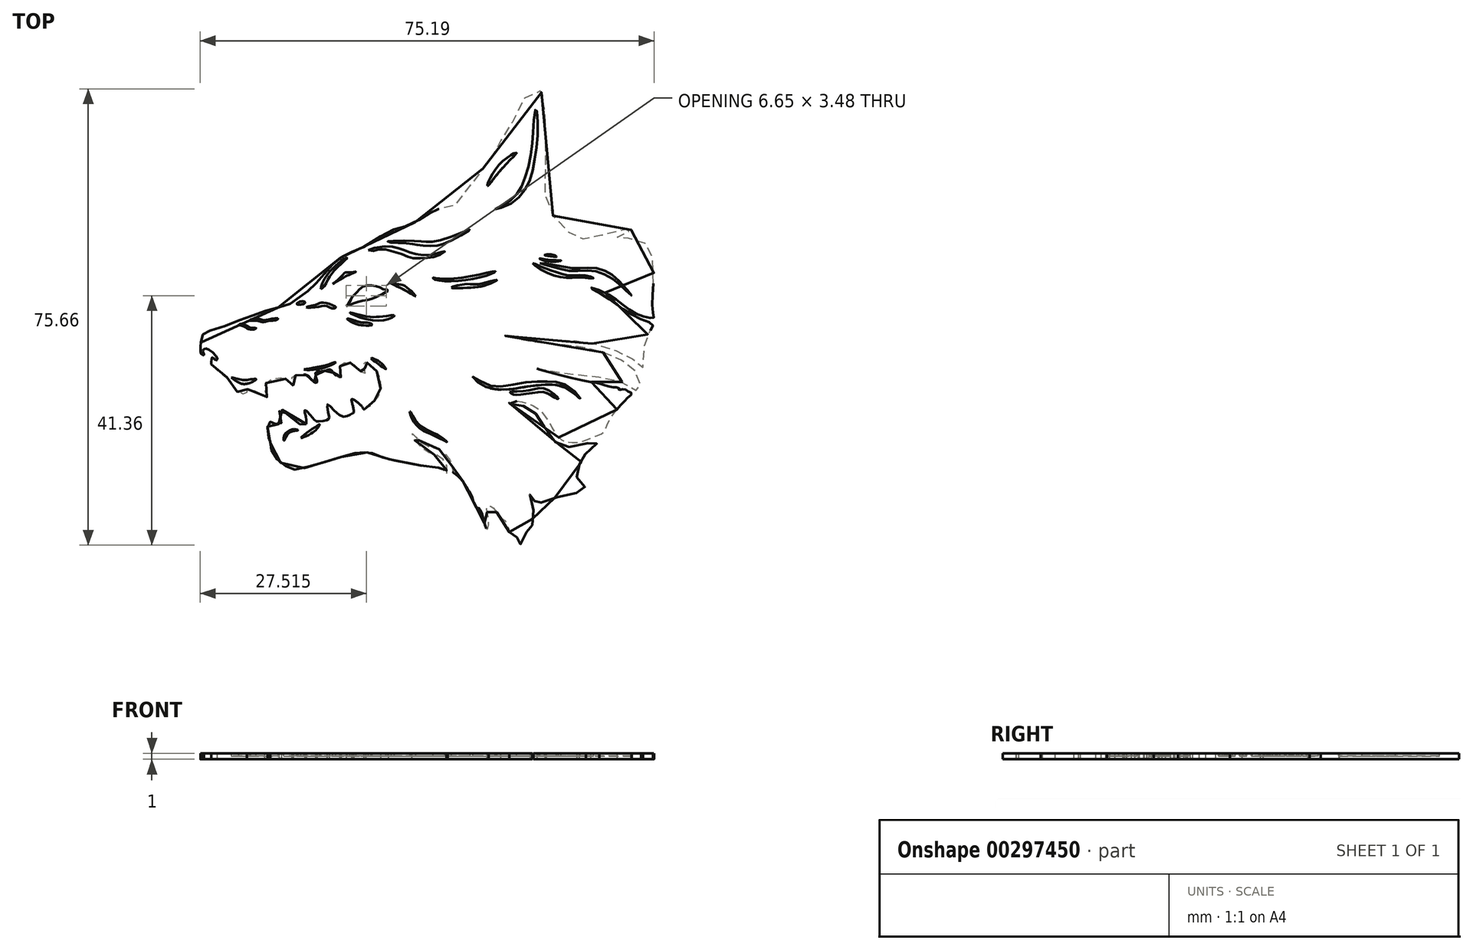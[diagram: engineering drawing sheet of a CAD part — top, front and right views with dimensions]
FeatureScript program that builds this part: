
annotation { "Feature Type Name" : "Feature", "Feature Type Description" : "" }
export const myFeature = defineFeature(function(context is Context, id is Id, definition is map)
    precondition{}
    {
        {
            var Q0;
            Q0=qCreatedBy(makeId("Top.planeOp"),FACE);
            var sketch = newSketch(context, id + "F0", { "sketchPlane" : qUnion([Q0])});
            skFitSpline(sketch, "E0", {"points": [v(1.7, 30.43) * mm, v(3.38, 28.83) * mm, v(5.2, 27.3) * mm, v(6.06, 25.78) * mm, v(7.8, 25.34) * mm, v(7.88, 25.85) * mm, v(8.31, 26.07) * mm, v(11.22, 24.76) * mm, v(11.07, 25.27) * mm, v(11, 27.01) * mm, v(13.61, 27.96) * mm, v(14.77, 27.3) * mm, v(15.35, 26.58) * mm, v(15.5, 26.58) * mm, v(15.35, 27.52) * mm, v(15.43, 28.18) * mm, v(16.37, 28.4) * mm, v(17, 28.43) * mm, v(17.55, 28.43) * mm, v(17.96, 28.27) * mm, v(18.59, 27.62) * mm, v(19.12, 27.13) * mm, v(19.44, 27.15) * mm, v(19.42, 27.68) * mm, v(19.24, 28.51) * mm, v(19.4, 28.9) * mm, v(20.48, 29.02) * mm, v(21.1, 29.22) * mm, v(21.7, 29.33) * mm, v(22.19, 28.8) * mm, v(22.7, 28.23) * mm, v(23.14, 27.94) * mm, v(23.4, 28.04) * mm, v(23.4, 28.65) * mm, v(23.25, 29.4) * mm, v(23.45, 30.14) * mm, v(24.26, 30.44) * mm, v(25.06, 30.42) * mm, v(26, 29.77) * mm, v(26.7, 29.04) * mm, v(27.2, 28.72) * mm, v(27.52, 28.72) * mm, v(27.39, 29.25) * mm, v(27.22, 30.2) * mm, v(27.4, 30.5) * mm, v(27.74, 30.5) * mm, v(28.42, 29.93) * mm, v(29.03, 29.46) * mm, v(29.87, 27.94) * mm, v(30.01, 26.04) * mm, v(29.78, 25) * mm, v(28.96, 24.06) * mm, v(28.41, 23.41) * mm, v(27.3, 22.69) * mm, v(26.95, 23.14) * mm, v(25.28, 24.38) * mm, v(25.2, 24.13) * mm, v(25.55, 22.14) * mm, v(25.18, 22.02) * mm], "startDerivative": vector(55.33, -59.39) * mm, "endDerivative": vector(-41.24, 3.28) * mm});
            skFitSpline(sketch, "E1", {"points": [v(25.34, 22) * mm, v(24.77, 21.7) * mm, v(23.5, 21.58) * mm, v(21.4, 23.42) * mm, v(21.16, 23.42) * mm, v(21.5, 21.3) * mm, v(21.36, 21.04) * mm, v(20.77, 20.78) * mm, v(19.52, 20.67) * mm, v(19.24, 20.76) * mm, v(17.57, 22.55) * mm, v(17.42, 22.5) * mm, v(17.6, 21.54) * mm, v(17.68, 20.28) * mm], "startDerivative": vector(-8.04, -4.42) * mm, "endDerivative": vector(-0.22, -13.93) * mm});
            skLineSegment(sketch, "E2", {"start": v(25.34, 22) * mm, "end": v(25.34, 22.01) * mm});
            skFitSpline(sketch, "E3", {"points": [v(27.3, 22.69) * mm, v(27.06, 22.75) * mm, v(25.28, 24.38) * mm, v(25.06, 24.13) * mm], "startDerivative": vector(-0.91, -0.23) * mm, "endDerivative": vector(-0.56, -1.9) * mm});
            skFitSpline(sketch, "E4", {"points": [v(17.68, 20.28) * mm, v(17.25, 20.09) * mm, v(16.58, 20.28) * mm, v(13.38, 22.77) * mm, v(13.2, 22.67) * mm, v(13.58, 20.69) * mm, v(13.43, 20.28) * mm, v(12.9, 20.28) * mm, v(12.33, 20.28) * mm, v(11.93, 20.59) * mm, v(11.4, 20.49) * mm, v(11.28, 19.71) * mm, v(11.43, 18.16) * mm, v(11.58, 17.84) * mm, v(11.73, 17.84) * mm, v(11.75, 17.36) * mm, v(11.78, 16.46) * mm, v(12.35, 15.14) * mm, v(13.43, 13.91) * mm, v(14.75, 12.99) * mm, v(15.85, 12.71) * mm, v(18.9, 13.41) * mm, v(22.66, 14.51) * mm, v(25.58, 15.39) * mm, v(27.16, 15.54) * mm, v(27.9, 15.54) * mm, v(28.7, 15.39) * mm, v(30.18, 14.76) * mm, v(32.2, 14.28) * mm, v(34.86, 13.7) * mm, v(37.27, 13.3) * mm, v(38.25, 13.16) * mm, v(38.84, 12.98) * mm, v(39.46, 13.03) * mm, v(40, 12.83) * mm, v(40.5, 12.57) * mm, v(41.02, 11.95) * mm, v(41.15, 11.95) * mm, v(40.94, 12.75) * mm, v(41.02, 13.4) * mm, v(40, 14.72) * mm, v(38.64, 15.29) * mm, v(37.14, 16.09) * mm, v(35.97, 17.28) * mm, v(35.5, 17.77) * mm, v(35.2, 18.55) * mm, v(35.35, 18.7) * mm, v(35.84, 18.08) * mm, v(37.06, 17) * mm, v(38.71, 16.3) * mm, v(39.52, 16.2) * mm, v(40.21, 15.7) * mm, v(41.07, 14.92) * mm, v(41.74, 13.78) * mm, v(41.92, 12.8) * mm, v(42, 12.3) * mm, v(42.85, 11.59) * mm, v(43.79, 10.58) * mm, v(44.33, 9.6) * mm, v(45, 8.6) * mm, v(45.85, 6.45) * mm, v(46.23, 6.34) * mm, v(46.85, 5.3) * mm, v(47.6, 2.81) * mm, v(47.74, 2.81) * mm, v(47.87, 4.86) * mm, v(47.6, 6.04) * mm, v(47.72, 6.58) * mm, v(48.1, 6.7) * mm, v(48.95, 6.04) * mm, v(50.1, 4.63) * mm, v(50.74, 4.07) * mm, v(51.38, 2.33) * mm], "startDerivative": vector(-47.47, -25.3) * mm, "endDerivative": vector(30.8, -113.8) * mm});
            skPoint(sketch, "E5.118.internal.snap0", {"position": v(76.24, 37.9) * mm});
            skPoint(sketch, "E5.119.internal.snap0", {"position": v(76.24, 37.9) * mm});
            skPoint(sketch, "E5.153.internal.snap0", {"position": v(38.12, 0) * mm});
            skPoint(sketch, "E5.171.internal.snap0", {"position": v(0, 37.9) * mm});
            skFitSpline(sketch, "E5", {"points": [v(51.38, 2.33) * mm, v(52.06, 2.33) * mm, v(52.36, 1.9) * mm, v(52.6, 1.43) * mm, v(52.8, 1.1) * mm, v(52.92, 0.25) * mm, v(53.12, 0.21) * mm, v(53.66, 1.5) * mm, v(54.07, 1.98) * mm, v(54.26, 2.58) * mm, v(54.75, 3.18) * mm, v(55.17, 3.35) * mm, v(55.18, 3.53) * mm, v(55.15, 4.7) * mm, v(55.38, 6.02) * mm, v(55.2, 6.95) * mm, v(54.78, 8.57) * mm, v(55.02, 8.81) * mm, v(55.33, 8.33) * mm, v(55.6, 7.3) * mm, v(55.76, 6.45) * mm, v(56.55, 7.16) * mm, v(58.12, 7.8) * mm, v(59.55, 8.21) * mm, v(61.96, 8.76) * mm, v(62.99, 9) * mm, v(64.02, 9.53) * mm, v(64, 9.7) * mm, v(63.32, 10.2) * mm, v(62.75, 10.43) * mm, v(62.63, 12.25) * mm, v(62.92, 12.68) * mm, v(62.97, 13.63) * mm, v(63.35, 14.04) * mm, v(63.6, 14.85) * mm, v(64.16, 15.5) * mm, v(64.65, 16.09) * mm, v(66.22, 17.33) * mm, v(66.22, 17.46) * mm, v(64.62, 17.15) * mm, v(62.85, 16.54) * mm, v(60.72, 16.52) * mm, v(59.68, 16.82) * mm, v(58.72, 17.5) * mm, v(57.5, 19.13) * mm, v(56.62, 20.79) * mm, v(55.91, 21.75) * mm, v(55.2, 22.49) * mm, v(54.24, 23.03) * mm, v(52.9, 23.5) * mm, v(51.74, 23.62) * mm, v(51.38, 23.67) * mm, v(51.38, 24.04) * mm, v(51.57, 24.02) * mm, v(52.59, 24.07) * mm, v(53.84, 23.86) * mm, v(55.35, 23.26) * mm, v(56.46, 22.53) * mm, v(57.38, 21.45) * mm, v(58.32, 19.91) * mm, v(58.98, 18.7) * mm, v(59.76, 17.81) * mm, v(60.85, 17.3) * mm, v(62.43, 17.2) * mm, v(63.94, 17.55) * mm, v(65.88, 18.33) * mm, v(67, 18.9) * mm, v(67.6, 20.17) * mm, v(68.26, 21.44) * mm, v(69.56, 23.1) * mm, v(71.1, 24.72) * mm, v(71.63, 25.37) * mm, v(70.94, 25.74) * mm, v(70.42, 26.04) * mm, v(69.6, 25.92) * mm, v(69.45, 26.25) * mm, v(68.92, 26.37) * mm, v(67.87, 26.46) * mm, v(66.33, 26.96) * mm, v(62.84, 27.6) * mm, v(55.94, 29.49) * mm, v(63, 28.3) * mm, v(67.4, 27.94) * mm, v(70.32, 27.1) * mm, v(72.16, 26.04) * mm, v(73.12, 25.23) * mm, v(72.97, 27.52) * mm, v(72.46, 28.68) * mm, v(71.48, 29.8) * mm, v(69.62, 31) * mm, v(67.3, 32) * mm, v(63.91, 32.9) * mm, v(60.82, 33.31) * mm, v(57.23, 33.66) * mm, v(54.97, 33.91) * mm, v(52.7, 34.32) * mm, v(51.38, 34.58) * mm, v(49.9, 35.43) * mm, v(52.1, 34.8) * mm, v(55.2, 34.36) * mm, v(58.96, 34.17) * mm, v(61.68, 34.1) * mm, v(64.09, 33.77) * mm, v(66.62, 33.26) * mm, v(69.45, 32.3) * mm, v(71.5, 31.35) * mm, v(73.33, 29.2) * mm, v(73.51, 31.1) * mm, v(73.96, 34.03) * mm, v(74.45, 35.4) * mm, v(75.14, 36.65) * mm, v(73.37, 37.6) * mm, v(69.77, 39.62) * mm, v(67.1, 41.51) * mm, v(64.83, 42.87) * mm, v(67.13, 42.07) * mm, v(70.06, 40.13) * mm, v(72.28, 38.62) * mm, v(74.52, 37.9) * mm, v(75.3, 37.9) * mm, v(75.1, 38.84) * mm, v(75.2, 42.72) * mm, v(75.13, 47.74) * mm, v(74.42, 49.57) * mm, v(73.55, 50.44) * mm, v(71.42, 51.03) * mm, v(69.94, 50.99) * mm, v(69.2, 51.12) * mm, v(70.02, 51.58) * mm, v(70.81, 52) * mm, v(71.7, 52.65) * mm, v(71.7, 52.88) * mm, v(69.55, 52.1) * mm, v(65.64, 51.41) * mm, v(63.64, 50.97) * mm, v(62.22, 50.87) * mm, v(60.24, 53.45) * mm, v(58.2, 55.28) * mm, v(57.23, 59.62) * mm, v(57.45, 64.42) * mm, v(57.28, 70.15) * mm, v(57.19, 73.48) * mm, v(56.14, 75.78) * mm, v(53.97, 74.4) * mm, v(51.79, 70.21) * mm, v(50.22, 67.75) * mm, v(48.96, 65.22) * mm, v(47.95, 64) * mm, v(45.85, 61.03) * mm, v(44.25, 59.06) * mm, v(42.77, 56.97) * mm, v(41.16, 55.92) * mm, v(39.46, 55.92) * mm, v(38.12, 55.2) * mm, v(36.36, 54.07) * mm, v(33.69, 52.9) * mm, v(31.9, 52.39) * mm, v(29.46, 51.03) * mm, v(28.44, 50.39) * mm, v(27.52, 49.75) * mm, v(25.48, 48.9) * mm, v(24.2, 48.35) * mm, v(22.65, 47.27) * mm, v(21.23, 45.8) * mm, v(19.86, 44.25) * mm, v(18.56, 42.79) * mm, v(17.36, 41.86) * mm, v(16.32, 41.1) * mm, v(14.69, 40.01) * mm, v(12.9, 39.55) * mm, v(10.55, 38.86) * mm, v(7.88, 37.9) * mm, v(5.5, 37.03) * mm, v(2.22, 35.83) * mm, v(0.84, 35.53) * mm, v(0.46, 34.75) * mm, v(0.27, 33.87) * mm, v(0, 32.43) * mm], "startDerivative": vector(214.49, 36.32) * mm, "endDerivative": vector(-54.5, -292.94) * mm});
            skFitSpline(sketch, "E6", {"points": [v(1.97, 30.14) * mm, v(2.02, 31.1) * mm, v(2.14, 31.3) * mm, v(2.7, 30.84) * mm, v(3, 31.03) * mm, v(1.38, 32.7) * mm, v(0.75, 32.7) * mm, v(0.58, 32.5) * mm, v(0.58, 32.2) * mm, v(0.73, 31.94) * mm, v(0.7, 31.69) * mm, v(0.5, 31.75) * mm, v(0.2, 32.2) * mm, v(0.25, 33.76) * mm], "startDerivative": vector(-0.09, 10.6) * mm, "endDerivative": vector(1.95, 14.03) * mm});
            skFitSpline(sketch, "E7", {"points": [v(5.25, 27.96) * mm, v(6.64, 27.07) * mm, v(7.44, 26.88) * mm, v(8.42, 27.07) * mm], "startDerivative": vector(3.66, -2.61) * mm, "endDerivative": vector(3.26, 0.84) * mm});
            skFitSpline(sketch, "E8", {"points": [v(8.42, 27.07) * mm, v(9.07, 27.42) * mm, v(9.4, 27.7) * mm, v(8.25, 27.63) * mm, v(7.2, 27.56) * mm, v(5.84, 27.87) * mm, v(5.25, 27.96) * mm], "startDerivative": vector(4.1, 2.1) * mm, "endDerivative": vector(-3.68, 0.4) * mm});
            skFitSpline(sketch, "E9", {"points": [v(6.54, 36.72) * mm, v(7.23, 36.5) * mm, v(8.01, 36.05) * mm, v(9.1, 35.95) * mm, v(9.4, 36.13) * mm, v(8.55, 36.2) * mm, v(8, 36.5) * mm, v(7.37, 36.76) * mm, v(7.06, 36.88) * mm, v(6.54, 36.72) * mm]});
            skFitSpline(sketch, "E10", {"points": [v(8.31, 37.42) * mm, v(9.56, 37.4) * mm, v(10.55, 37.12) * mm, v(11.41, 37.34) * mm, v(12.34, 37.42) * mm, v(13.04, 37.72) * mm, v(12.01, 37.74) * mm, v(10.79, 37.48) * mm, v(9.88, 37.68) * mm, v(8.88, 37.7) * mm, v(8.31, 37.42) * mm]});
            skFitSpline(sketch, "E11", {"points": [v(16.13, 40.18) * mm, v(17.12, 40.14) * mm, v(17.5, 40.4) * mm, v(17.03, 40.61) * mm, v(16.13, 40.18) * mm]});
            skFitSpline(sketch, "E12", {"points": [v(17.72, 39.62) * mm, v(19.31, 39.62) * mm, v(20.95, 39.88) * mm, v(22.16, 39.4) * mm, v(22.59, 39.62) * mm, v(21.2, 40.27) * mm, v(20.09, 40.4) * mm, v(19.44, 40.1) * mm, v(17.72, 39.62) * mm]});
            skFitSpline(sketch, "E13", {"points": [v(24.48, 37.68) * mm, v(25.99, 36.82) * mm, v(27.37, 36.6) * mm, v(28.61, 36.7) * mm, v(28.06, 37.04) * mm, v(26.94, 37.08) * mm, v(25.26, 37.56) * mm, v(24.48, 37.68) * mm]});
            skFitSpline(sketch, "E14", {"points": [v(20.14, 42.7) * mm, v(20.78, 44.41) * mm, v(22.43, 46.42) * mm, v(23.8, 47.5) * mm, v(24.5, 47.82) * mm, v(22.9, 46.28) * mm, v(21.46, 44.52) * mm, v(20.57, 42.98) * mm, v(20.14, 42.7) * mm]});
            skFitSpline(sketch, "E15", {"points": [v(24.33, 39.8) * mm, v(25.08, 40.11) * mm, v(26.44, 40.54) * mm, v(28.05, 40.9) * mm, v(29.34, 41.37) * mm, v(31.31, 42.48) * mm, v(30.67, 42.55) * mm, v(29.77, 42.94) * mm, v(28.73, 43.23) * mm, v(27.34, 43.16) * mm, v(26.37, 42.48) * mm, v(25.69, 41.69) * mm, v(25.22, 41.26) * mm, v(24.97, 40.54) * mm, v(24.33, 39.8) * mm]});
            skFitSpline(sketch, "E16", {"points": [v(22.07, 43.48) * mm, v(23.5, 44.7) * mm, v(24.15, 45.38) * mm, v(24.8, 45.38) * mm, v(25.94, 45.52) * mm, v(24.86, 45.02) * mm, v(24.08, 44.66) * mm, v(22.07, 43.48) * mm]});
            skFitSpline(sketch, "E17", {"points": [v(24.97, 38.72) * mm, v(27.3, 38.18) * mm, v(29.16, 38) * mm, v(30.7, 38.14) * mm, v(32.32, 38.25) * mm, v(31.57, 37.71) * mm, v(27.3, 37.75) * mm, v(24.97, 38.72) * mm]});
            skFitSpline(sketch, "E18", {"points": [v(35.86, 41.44) * mm, v(34.4, 42.9) * mm, v(33.07, 43.45) * mm, v(31.78, 43.59) * mm, v(34.04, 42.48) * mm, v(35.86, 41.44) * mm]});
            skFitSpline(sketch, "E19", {"points": [v(28.01, 49.07) * mm, v(28.88, 48.99) * mm, v(29.96, 49.23) * mm, v(32.1, 48.88) * mm, v(34.24, 48.15) * mm, v(35.22, 47.8) * mm, v(36.99, 47.75) * mm, v(38.53, 47.88) * mm, v(40.09, 48.45) * mm, v(40.69, 48.95) * mm, v(38.8, 48.37) * mm, v(36.3, 48.37) * mm, v(34.98, 48.66) * mm, v(33.68, 49.2) * mm, v(32.35, 49.56) * mm, v(30.4, 49.69) * mm, v(28.01, 49.07) * mm]});
            skFitSpline(sketch, "E20", {"points": [v(31.23, 50.53) * mm, v(35.48, 50.64) * mm, v(37.47, 50.47) * mm, v(40.51, 50.9) * mm, v(44.9, 52.52) * mm, v(41.32, 50.53) * mm, v(38.93, 49.83) * mm, v(36.29, 49.94) * mm, v(35.08, 50.15) * mm, v(31.95, 50.34) * mm, v(31.23, 50.53) * mm]});
            skFitSpline(sketch, "E21", {"points": [v(47.75, 59.77) * mm, v(49.5, 63.08) * mm, v(52.56, 65.23) * mm, v(50.04, 62.5) * mm, v(47.75, 59.77) * mm]});
            skFitSpline(sketch, "E22", {"points": [v(49, 55.89) * mm, v(50.87, 56.45) * mm, v(53.33, 58.26) * mm, v(54.88, 61.07) * mm, v(55.7, 65.04) * mm, v(56.1, 70) * mm, v(55.75, 72.56) * mm, v(55.4, 70) * mm, v(55.06, 65.78) * mm, v(54.1, 61.54) * mm, v(52.94, 58.87) * mm, v(51.17, 57.1) * mm, v(49, 55.89) * mm]});
            skFitSpline(sketch, "E23", {"points": [v(39.04, 44.23) * mm, v(43.18, 44.03) * mm, v(48.28, 45.11) * mm, v(49.04, 45.57) * mm, v(44.14, 44.62) * mm, v(39.18, 44.42) * mm, v(38.69, 44.5) * mm, v(39.04, 44.23) * mm]});
            skFitSpline(sketch, "E24", {"points": [v(41.8, 42.87) * mm, v(44.65, 42.85) * mm, v(47.65, 43.34) * mm, v(49.3, 44.15) * mm, v(46.19, 43.46) * mm, v(44.14, 43.46) * mm, v(41.8, 42.87) * mm]});
            skFitSpline(sketch, "E25", {"points": [v(57.21, 48.28) * mm, v(58.28, 48.38) * mm, v(59.18, 48.01) * mm, v(58.11, 48.11) * mm, v(57.21, 48.28) * mm]});
            skFitSpline(sketch, "E26", {"points": [v(56.34, 47.68) * mm, v(57.98, 47.2) * mm, v(59.95, 47.34) * mm, v(57.95, 47.48) * mm, v(56.34, 47.68) * mm]});
            skFitSpline(sketch, "E27", {"points": [v(56.44, 46.94) * mm, v(59.58, 46.04) * mm, v(61.81, 45.64) * mm, v(64.38, 45.7) * mm, v(66.42, 45.38) * mm, v(68.72, 44.17) * mm, v(70.18, 42.84) * mm, v(71.62, 41.57) * mm, v(69.82, 43.7) * mm, v(67.95, 45.28) * mm, v(65.95, 46.04) * mm, v(63.82, 46.18) * mm, v(62.11, 46.1) * mm, v(59.85, 46.4) * mm, v(57.85, 46.8) * mm, v(56.44, 46.94) * mm]});
            skFitSpline(sketch, "E28", {"points": [v(55.24, 46.9) * mm, v(57.21, 45.54) * mm, v(60.55, 44.54) * mm, v(63.48, 44.54) * mm, v(65.32, 44.4) * mm, v(63.98, 44.9) * mm, v(61.45, 44.88) * mm, v(58.75, 45.58) * mm, v(56.58, 46.38) * mm, v(55.24, 46.9) * mm]});
            skFitSpline(sketch, "E29", {"points": [v(45.34, 28.08) * mm, v(47.3, 26.97) * mm, v(50.14, 26.53) * mm, v(54.2, 27.18) * mm, v(57.24, 27.27) * mm, v(59.24, 27.21) * mm, v(61.8, 26.05) * mm, v(63.12, 24.5) * mm, v(61.27, 25.93) * mm, v(59.12, 26.73) * mm, v(56.35, 26.7) * mm, v(53.27, 26.29) * mm, v(50.4, 25.96) * mm, v(48.17, 26.2) * mm, v(46.47, 26.91) * mm, v(45.34, 28.08) * mm]});
            skFitSpline(sketch, "E30", {"points": [v(51.4, 25.6) * mm, v(52.77, 25.63) * mm, v(55.72, 26.1) * mm, v(57.78, 25.93) * mm, v(59.48, 24.44) * mm, v(58.32, 24.97) * mm, v(57.12, 25.54) * mm, v(54.53, 25.33) * mm, v(52.35, 25.1) * mm, v(51.84, 25.21) * mm, v(51.4, 25.6) * mm]});
            skFitSpline(sketch, "E31", {"points": [v(34.95, 22.31) * mm, v(36.15, 20.45) * mm, v(37.73, 19.25) * mm, v(39.62, 18.37) * mm, v(41.07, 17.28) * mm, v(39.6, 17.98) * mm, v(37.83, 18.8) * mm, v(36.49, 19.55) * mm, v(35.29, 21) * mm, v(34.85, 22.38) * mm], "startDerivative": vector(8.84, -16.2) * mm, "endDerivative": vector(-2.93, 13.91) * mm});
            skLineSegment(sketch, "E32", {"start": v(34.95, 22.31) * mm, "end": v(34.85, 22.38) * mm});
            skFitSpline(sketch, "E33", {"points": [v(28.44, 31.15) * mm, v(29.72, 30.68) * mm, v(30.89, 29.35) * mm, v(29.6, 30.25) * mm, v(28.44, 31.15) * mm]});
            skFitSpline(sketch, "E34", {"points": [v(16.83, 17.97) * mm, v(18.45, 18.63) * mm, v(19.54, 19.57) * mm, v(19.92, 20.19) * mm, v(18.24, 19.1) * mm, v(16.83, 17.97) * mm]});
            skFitSpline(sketch, "E35", {"points": [v(13.94, 17.7) * mm, v(14.08, 18.48) * mm, v(14.8, 19.08) * mm, v(15.7, 19.43) * mm, v(16.34, 19.23) * mm, v(15.42, 19.02) * mm, v(14.41, 18.3) * mm, v(14.01, 17.52) * mm, v(13.94, 17.7) * mm]});
            skFitSpline(sketch, "E36", {"points": [v(17.35, 29.31) * mm, v(20.15, 29.82) * mm, v(22.58, 30.49) * mm, v(20.1, 29.45) * mm, v(17.35, 29.31) * mm]});
            skSolve(sketch);
        }
        {
            var Q0;
            Q0 = qSketchRegion(id + "F0", true);
            extrude(context, id + "F1", {"entities" : qUnion([Q0]), "depth" : 1 * mm});
        }
        {
            var Q0;
            Q0=makeQuery(id+"F0.imprint","IMPRINT",FACE,{"disambiguationData":[TD([[makeQuery(id+"F0.imprint","IMPRINT",EDGE,{"derivedFrom":sQuery(id+"F0.wireOp",EDGE,"E16")}),-1.0]])]});
            var Q1;
            Q1=makeQuery(id+"F0.imprint","IMPRINT",FACE,{"disambiguationData":[TD([[makeQuery(id+"F0.imprint","IMPRINT",EDGE,{"derivedFrom":sQuery(id+"F0.wireOp",EDGE,"E14")}),-1.0]])]});
            var Q2;
            Q2=makeQuery(id+"F0.imprint","IMPRINT",FACE,{"disambiguationData":[TD([[makeQuery(id+"F0.imprint","IMPRINT",EDGE,{"derivedFrom":sQuery(id+"F0.wireOp",EDGE,"E18")}),1.0]])]});
            var Q3;
            Q3=makeQuery(id+"F0.imprint","IMPRINT",FACE,{"disambiguationData":[TD([[makeQuery(id+"F0.imprint","IMPRINT",EDGE,{"derivedFrom":sQuery(id+"F0.wireOp",EDGE,"E19")}),1.0]])]});
            var Q4;
            Q4=makeQuery(id+"F0.imprint","IMPRINT",FACE,{"disambiguationData":[TD([[makeQuery(id+"F0.imprint","IMPRINT",EDGE,{"derivedFrom":sQuery(id+"F0.wireOp",EDGE,"E20")}),-1.0]])]});
            var Q5;
            Q5=makeQuery(id+"F0.imprint","IMPRINT",FACE,{"disambiguationData":[TD([[makeQuery(id+"F0.imprint","IMPRINT",EDGE,{"derivedFrom":sQuery(id+"F0.wireOp",EDGE,"E23")}),1.0]])]});
            var Q6;
            Q6=makeQuery(id+"F0.imprint","IMPRINT",FACE,{"disambiguationData":[TD([[makeQuery(id+"F0.imprint","IMPRINT",EDGE,{"derivedFrom":sQuery(id+"F0.wireOp",EDGE,"E24")}),1.0]])]});
            var Q7;
            Q7=makeQuery(id+"F0.imprint","IMPRINT",FACE,{"disambiguationData":[TD([[makeQuery(id+"F0.imprint","IMPRINT",EDGE,{"derivedFrom":sQuery(id+"F0.wireOp",EDGE,"E17")}),-1.0]])]});
            var Q8;
            Q8=makeQuery(id+"F0.imprint","IMPRINT",FACE,{"disambiguationData":[TD([[makeQuery(id+"F0.imprint","IMPRINT",EDGE,{"derivedFrom":sQuery(id+"F0.wireOp",EDGE,"E13")}),1.0]])]});
            var Q9;
            Q9=makeQuery(id+"F0.imprint","IMPRINT",FACE,{"disambiguationData":[TD([[makeQuery(id+"F0.imprint","IMPRINT",EDGE,{"derivedFrom":sQuery(id+"F0.wireOp",EDGE,"E12")}),1.0]])]});
            var Q10;
            Q10=makeQuery(id+"F0.imprint","IMPRINT",FACE,{"disambiguationData":[TD([[makeQuery(id+"F0.imprint","IMPRINT",EDGE,{"derivedFrom":sQuery(id+"F0.wireOp",EDGE,"E10")}),1.0]])]});
            var Q11;
            Q11=makeQuery(id+"F0.imprint","IMPRINT",FACE,{"disambiguationData":[TD([[makeQuery(id+"F0.imprint","IMPRINT",EDGE,{"derivedFrom":sQuery(id+"F0.wireOp",EDGE,"E9")}),1.0]])]});
            var Q12;
            Q12=makeQuery(id+"F0.imprint","IMPRINT",FACE,{"disambiguationData":[TD([[makeQuery(id+"F0.imprint","IMPRINT",EDGE,{"derivedFrom":sQuery(id+"F0.wireOp",EDGE,"E7")}),1.0]])]});
            var Q13;
            Q13=makeQuery(id+"F0.imprint","IMPRINT",FACE,{"disambiguationData":[TD([[makeQuery(id+"F0.imprint","IMPRINT",EDGE,{"derivedFrom":sQuery(id+"F0.wireOp",EDGE,"E36")}),-1.0]])]});
            var Q14;
            Q14=makeQuery(id+"F0.imprint","IMPRINT",FACE,{"disambiguationData":[TD([[makeQuery(id+"F0.imprint","IMPRINT",EDGE,{"derivedFrom":sQuery(id+"F0.wireOp",EDGE,"E33")}),-1.0]])]});
            var Q15;
            Q15=makeQuery(id+"F0.imprint","IMPRINT",FACE,{"disambiguationData":[TD([[makeQuery(id+"F0.imprint","IMPRINT",EDGE,{"derivedFrom":sQuery(id+"F0.wireOp",EDGE,"E34")}),1.0]])]});
            var Q16;
            Q16=makeQuery(id+"F0.imprint","IMPRINT",FACE,{"disambiguationData":[TD([[makeQuery(id+"F0.imprint","IMPRINT",EDGE,{"derivedFrom":sQuery(id+"F0.wireOp",EDGE,"E35")}),-1.0]])]});
            var Q17;
            Q17=makeQuery(id+"F0.imprint","IMPRINT",FACE,{"disambiguationData":[TD([[makeQuery(id+"F0.imprint","IMPRINT",EDGE,{"derivedFrom":sQuery(id+"F0.wireOp",EDGE,"E31")}),-1.0]])]});
            var Q18;
            Q18=makeQuery(id+"F0.imprint","IMPRINT",FACE,{"disambiguationData":[TD([[makeQuery(id+"F0.imprint","IMPRINT",EDGE,{"derivedFrom":sQuery(id+"F0.wireOp",EDGE,"E29")}),-1.0]])]});
            var Q19;
            Q19=makeQuery(id+"F0.imprint","IMPRINT",FACE,{"disambiguationData":[TD([[makeQuery(id+"F0.imprint","IMPRINT",EDGE,{"derivedFrom":sQuery(id+"F0.wireOp",EDGE,"E30")}),-1.0]])]});
            var Q20;
            Q20=makeQuery(id+"F0.imprint","IMPRINT",FACE,{"disambiguationData":[TD([[makeQuery(id+"F0.imprint","IMPRINT",EDGE,{"derivedFrom":sQuery(id+"F0.wireOp",EDGE,"E28")}),1.0]])]});
            var Q21;
            Q21=makeQuery(id+"F0.imprint","IMPRINT",FACE,{"disambiguationData":[TD([[makeQuery(id+"F0.imprint","IMPRINT",EDGE,{"derivedFrom":sQuery(id+"F0.wireOp",EDGE,"E27")}),1.0]])]});
            var Q22;
            Q22=makeQuery(id+"F0.imprint","IMPRINT",FACE,{"disambiguationData":[TD([[makeQuery(id+"F0.imprint","IMPRINT",EDGE,{"derivedFrom":sQuery(id+"F0.wireOp",EDGE,"E26")}),1.0]])]});
            var Q23;
            Q23=makeQuery(id+"F0.imprint","IMPRINT",FACE,{"disambiguationData":[TD([[makeQuery(id+"F0.imprint","IMPRINT",EDGE,{"derivedFrom":sQuery(id+"F0.wireOp",EDGE,"E21")}),-1.0]])]});
            var Q24;
            Q24=makeQuery(id+"F0.imprint","IMPRINT",FACE,{"disambiguationData":[TD([[makeQuery(id+"F0.imprint","IMPRINT",EDGE,{"derivedFrom":sQuery(id+"F0.wireOp",EDGE,"E22")}),1.0]])]});
            var Q25;
            Q25=makeQuery(id+"F0.imprint","IMPRINT",FACE,{"disambiguationData":[TD([[makeQuery(id+"F0.imprint","IMPRINT",EDGE,{"derivedFrom":sQuery(id+"F0.wireOp",EDGE,"E25")}),-1.0]])]});
            var Q26;
            Q26=makeQuery(id+"F0.imprint","IMPRINT",FACE,{"disambiguationData":[TD([[makeQuery(id+"F0.imprint","IMPRINT",EDGE,{"derivedFrom":sQuery(id+"F0.wireOp",EDGE,"E11")}),1.0]])]});
            extrude(context, id + "F2", {"entities" : qUnion([Q0, Q1, Q2, Q3, Q4, Q5, Q6, Q7, Q8, Q9, Q10, Q11, Q12, Q13, Q14, Q15, Q16, Q17, Q18, Q19, Q20, Q21, Q22, Q23, Q24, Q25, Q26]), "operationType" : NewBodyOperationType.ADD, "depth" : 0.5 * mm});
        }
    });
